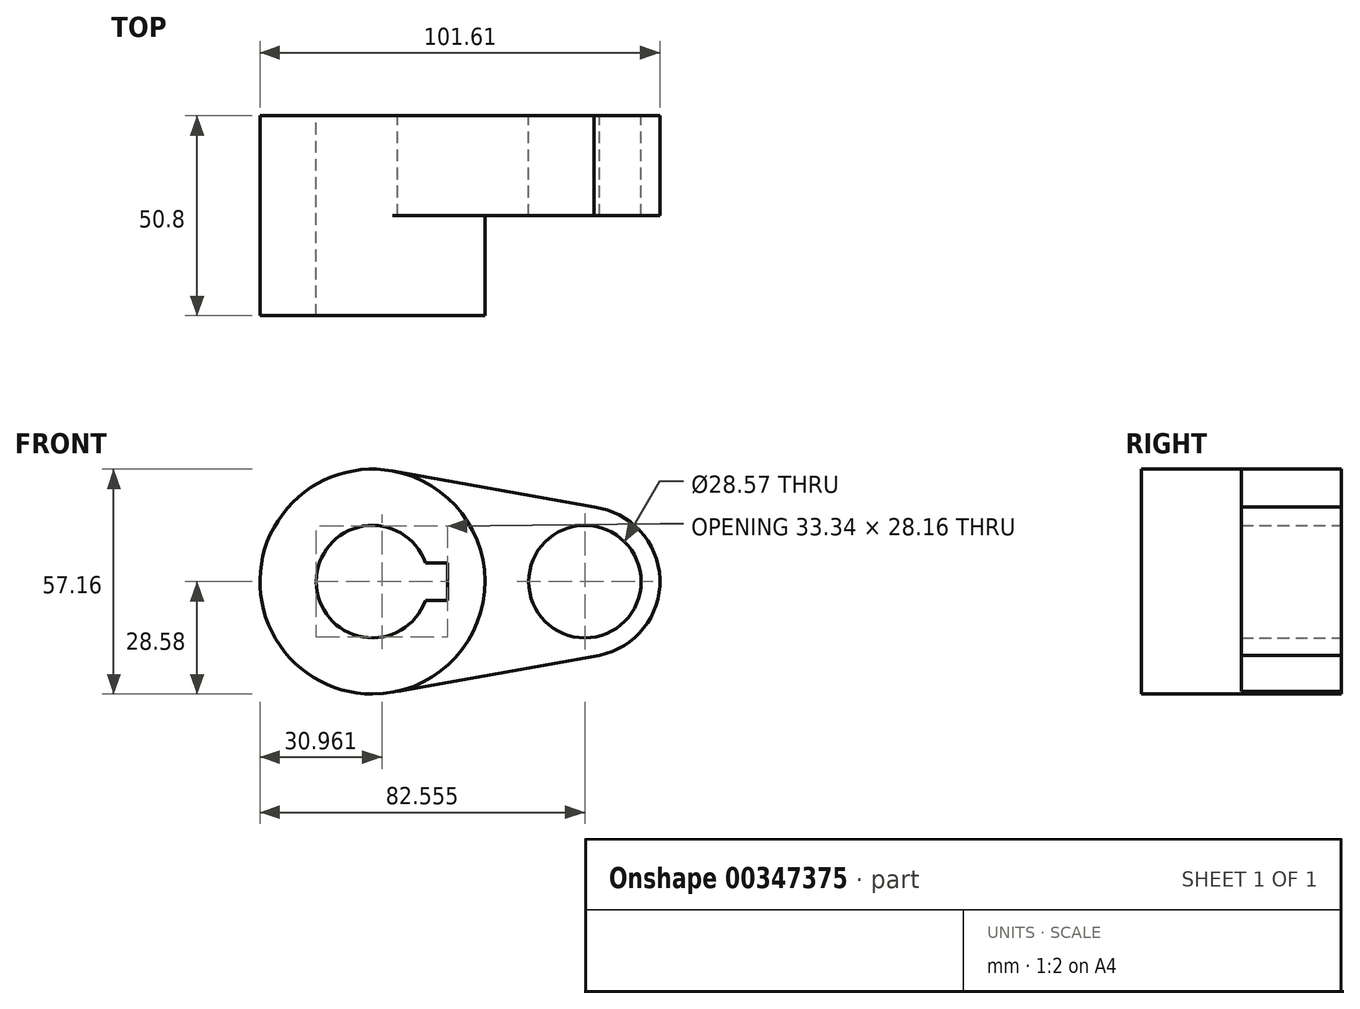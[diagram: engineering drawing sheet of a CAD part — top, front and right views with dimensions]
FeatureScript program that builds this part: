
annotation { "Feature Type Name" : "Feature", "Feature Type Description" : "" }
export const myFeature = defineFeature(function(context is Context, id is Id, definition is map)
    precondition{}
    {
        {
            var Q0;
            Q0=qCreatedBy(makeId("Front.planeOp"),FACE);
            var sketch = newSketch(context, id + "F0", { "sketchPlane" : qUnion([Q0])});
            skCircle(sketch, "E0", {"center": v(0, 0) * mm, "radius": 28.58 * mm});
            skCircle(sketch, "E1", {"center": v(53.98, 0) * mm, "radius": 19.05 * mm});
            skCircle(sketch, "E2", {"center": v(0, 0) * mm, "radius": 14.29 * mm});
            skCircle(sketch, "E3", {"center": v(53.98, 0) * mm, "radius": 14.29 * mm});
            skLineSegment(sketch, "E4.bottom", {"start": v(19.05, -4.76) * mm, "end": v(-19.05, -4.76) * mm});
            skLineSegment(sketch, "E4.top", {"start": v(19.05, 4.76) * mm, "end": v(-19.05, 4.76) * mm});
            skLineSegment(sketch, "E4.left", {"start": v(19.05, -4.76) * mm, "end": v(19.05, 4.76) * mm});
            skLineSegment(sketch, "E4.right", {"start": v(-19.05, -4.76) * mm, "end": v(-19.05, 4.76) * mm});
            skLineSegment(sketch, "E5", {"start": v(5.06, 28.12) * mm, "end": v(56.29, 18.9) * mm});
            skLineSegment(sketch, "E6", {"start": v(6.41, -27.85) * mm, "end": v(57.65, -18.7) * mm});
            skSolve(sketch);
        }
        {
            var Q0;
            {var subQ11=sQuery(id+"F0.wireOp",EDGE,"E4.left");Q0=makeQuery(id+"F0.imprint","IMPRINT",FACE,{"disambiguationData":[TD([[makeQuery(id+"F0.imprint","IMPRINT",EDGE,{"derivedFrom":subQ11}),-1.0]])]});}
            var Q1;
            {var subQ5=sQuery(id+"F0.wireOp",EDGE,"E4.right");Q1=makeQuery(id+"F0.imprint","IMPRINT",FACE,{"disambiguationData":[TD([[makeQuery(id+"F0.imprint","IMPRINT",EDGE,{"derivedFrom":subQ5}),-1.0]])]});}
            var Q2;
            {var subQ0=sQuery(id+"F0.wireOp",EDGE,"E5");Q2=makeQuery(id+"F0.imprint","IMPRINT",FACE,{"disambiguationData":[TD([[makeQuery(id+"F0.imprint","IMPRINT",EDGE,{"derivedFrom":subQ0}),-1.0]])]});}
            var Q3;
            Q3=makeQuery(id+"F0.imprint","IMPRINT",FACE,{"disambiguationData":[TD([[makeQuery(id+"F0.imprint","IMPRINT",EDGE,{"derivedFrom":sQuery(id+"F0.wireOp",EDGE,"E3")}),-1.0]])]});
            extrude(context, id + "F1", {"entities" : qUnion([Q0, Q1, Q2, Q3]), "depth" : 25.4 * mm});
        }
        {
            var Q0;
            {var subQ11=sQuery(id+"F0.wireOp",EDGE,"E4.left");Q0=makeQuery(id+"F0.imprint","IMPRINT",FACE,{"disambiguationData":[TD([[makeQuery(id+"F0.imprint","IMPRINT",EDGE,{"derivedFrom":subQ11}),-1.0]])]});}
            var Q1;
            {var subQ5=sQuery(id+"F0.wireOp",EDGE,"E4.right");Q1=makeQuery(id+"F0.imprint","IMPRINT",FACE,{"disambiguationData":[TD([[makeQuery(id+"F0.imprint","IMPRINT",EDGE,{"derivedFrom":subQ5}),-1.0]])]});}
            extrude(context, id + "F2", {"entities" : qUnion([Q0, Q1]), "operationType" : NewBodyOperationType.ADD, "depth" : 50.8 * mm});
        }
    });
